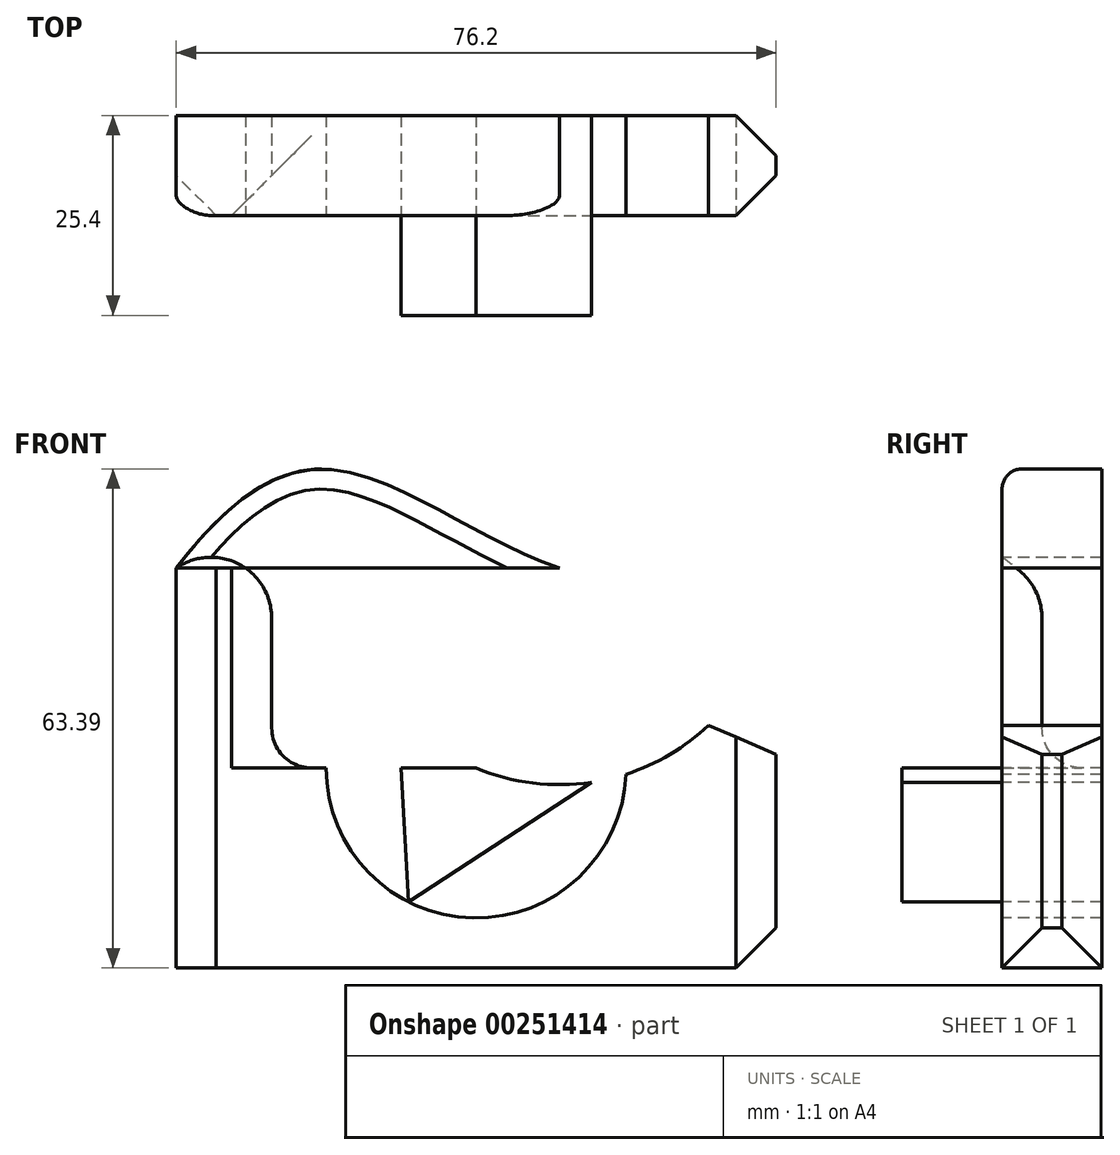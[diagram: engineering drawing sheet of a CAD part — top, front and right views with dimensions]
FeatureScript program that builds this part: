
annotation { "Feature Type Name" : "Feature", "Feature Type Description" : "" }
export const myFeature = defineFeature(function(context is Context, id is Id, definition is map)
    precondition{}
    {
        {
            var Q0;
            Q0=qCreatedBy(makeId("Front.planeOp"),FACE);
            var sketch = newSketch(context, id + "F0", { "sketchPlane" : qUnion([Q0])});
            skLineSegment(sketch, "E0.bottom", {"start": v(0, 0) * mm, "end": v(-25.97, 0) * mm});
            skLineSegment(sketch, "E0.top", {"start": v(0, 19.05) * mm, "end": v(-25.97, 19.05) * mm});
            skLineSegment(sketch, "E0.left", {"start": v(0, 0) * mm, "end": v(0, 19.05) * mm});
            skLineSegment(sketch, "E0.right", {"start": v(-25.97, 0) * mm, "end": v(-25.97, 19.05) * mm});
            skLineSegment(sketch, "E1.bottom", {"start": v(-38.1, 25.4) * mm, "end": v(38.1, 25.4) * mm});
            skLineSegment(sketch, "E1.top", {"start": v(-38.1, -25.4) * mm, "end": v(38.1, -25.4) * mm});
            skLineSegment(sketch, "E1.left", {"start": v(-38.1, 25.4) * mm, "end": v(-38.1, -25.4) * mm});
            skLineSegment(sketch, "E1.right", {"start": v(38.1, 25.4) * mm, "end": v(38.1, -25.4) * mm});
            skPoint(sketch, "E1.middle", {"position": v(0, 0) * mm});
            skCircle(sketch, "E2", {"center": v(0, 0) * mm, "radius": 19.05 * mm});
            skArc(sketch, "E3", {"start": v(0, 0) * mm, "mid": v(25.85, 2.5) * mm, "end": v(38.1, 25.4) * mm});
            skFitSpline(sketch, "E4", {"points": [v(-38.1, 25.4) * mm, v(-18.99, 37.97) * mm, v(10.58, 25.4) * mm, v(38.1, 25.4) * mm], "startDerivative": vector(56.09, 72.13) * mm, "endDerivative": vector(78.9, 16.08) * mm});
            skArc(sketch, "E5", {"start": v(-25.97, 19.05) * mm, "mid": v(-30.11, 25.9) * mm, "end": v(-38.1, 25.4) * mm});
            skCircle(sketch, "E6.cCircle", {"center": v(0, 0) * mm, "radius": 19.05 * mm, "construction": true});
            skLineSegment(sketch, "E6.0", {"start": v(19.02, 1.05) * mm, "end": v(-8.6, -17) * mm});
            skLineSegment(sketch, "E6.1", {"start": v(-8.6, -17) * mm, "end": v(-10.42, 15.95) * mm});
            skLineSegment(sketch, "E6.2", {"start": v(-10.42, 15.95) * mm, "end": v(19.02, 1.05) * mm});
            skSolve(sketch);
        }
        {
            var Q0;
            {var subQ1=sQuery(id+"F0.wireOp",EDGE,"E0.bottom");var subQ3=sQuery(id+"F0.wireOp",EDGE,"E6.1");var subQ4=makeQuery(id+"F0.imprint","INTERSECT",VERTEX,{"derivedFrom":[subQ1,subQ3]});Q0=makeQuery(id+"F0.imprint","IMPRINT",FACE,{"disambiguationData":[TD([[makeQuery(id+"F0.imprint","IMPRINT",EDGE,{"disambiguationData":[TD([[subQ4,1.0]])],"derivedFrom":subQ1}),1.0]])]});}
            var Q1;
            {var subQ5=sQuery(id+"F0.wireOp",EDGE,"E0.right");Q1=makeQuery(id+"F0.imprint","IMPRINT",FACE,{"disambiguationData":[TD([[makeQuery(id+"F0.imprint","IMPRINT",EDGE,{"derivedFrom":subQ5}),1.0]])]});}
            var Q2;
            {var subQ0=sQuery(id+"F0.wireOp",EDGE,"E4");var subQ1=sQuery(id+"F0.wireOp",EDGE,"E1.bottom");var subQ2=makeQuery(id+"F0.imprint","INTERSECT",VERTEX,{"derivedFrom":[subQ1,subQ0]});Q2=makeQuery(id+"F0.imprint","IMPRINT",FACE,{"disambiguationData":[TD([[makeQuery(id+"F0.imprint","IMPRINT",EDGE,{"disambiguationData":[TD([[subQ2,1.0]])],"derivedFrom":subQ1}),1.0]])]});}
            extrude(context, id + "F1", {"entities" : qUnion([Q0, Q1, Q2]), "oppositeDirection" : true, "depth" : 12.7 * mm});
        }
        {
            var Q0;
            Q0=makeQuery(id+"F1.opExtrude","CAP_FACE",FACE,{"disambiguationData":[OSD([sQuery(id+"F0.wireOp",EDGE,"E0.bottom"),sQuery(id+"F0.wireOp",EDGE,"E3"),sQuery(id+"F0.wireOp",EDGE,"E6.0"),sQuery(id+"F0.wireOp",EDGE,"E6.1")])],"isStart":false});
            extrude(context, id + "F2", {"entities" : qUnion([Q0]), "operationType" : NewBodyOperationType.ADD, "oppositeDirection" : true, "depth" : 25.4 * mm});
        }
        {
            var Q0;
            Q0=makeQuery(id+"F1.opExtrude","CAP_EDGE",EDGE,{"disambiguationData":[OSD([sQuery(id+"F0.wireOp",EDGE,"E4")])],"isStart":true});
            fillet(context, id + "F3", {"entities" : qUnion([Q0]), "radius" : 2.54 * mm, "tangentPropagation" : true, "allowEdgeOverflow" : false});
        }
        {
            var Q0;
            Q0=makeQuery(id+"F1.opExtrude","SWEPT_FACE",FACE,{"disambiguationData":[OSD([sQuery(id+"F0.wireOp",EDGE,"E1.right")])]});
            var Q1;
            Q1=makeQuery(id+"F1.opExtrude","CAP_EDGE",EDGE,{"disambiguationData":[OSD([sQuery(id+"F0.wireOp",EDGE,"E1.right")])],"isStart":false});
            var Q2;
            {var subQ0=sQuery(id+"F0.wireOp",EDGE,"E5");Q2=makeQuery(id+"F1.opExtrude","CAP_EDGE",EDGE,{"disambiguationData":[OSD([subQ0]),TDD([makeQuery(id+"F0.imprint","IMPRINT",EDGE,{"disambiguationData":[TD([[makeQuery(id+"F0.imprint","INTERSECT",VERTEX,{"derivedFrom":[sQuery(id+"F0.wireOp",EDGE,"E1.bottom"),subQ0]}),1.0]])],"derivedFrom":subQ0})])],"isStart":true});}
            chamfer(context, id + "F4", {"entities" : qUnion([Q0, Q1, Q2]), "width" : 5.08 * mm, "tangentPropagation" : true});
        }
        {
            var Q0;
            Q0=makeQuery(id+"F1.opExtrude","CAP_EDGE",EDGE,{"disambiguationData":[OSD([sQuery(id+"F0.wireOp",EDGE,"E1.left")])],"isStart":true});
            chamfer(context, id + "F5", {"entities" : qUnion([Q0]), "width" : 5.08 * mm, "tangentPropagation" : true});
        }
        {
            var Q0;
            Q0=makeQuery(id+"F1.opExtrude","SWEPT_EDGE",EDGE,{"disambiguationData":[OSD([sQuery(id+"F0.wireOp",EDGE,"E0.bottom"),sQuery(id+"F0.wireOp",EDGE,"E0.right")])]});
            fillet(context, id + "F6", {"entities" : qUnion([Q0]), "radius" : 5.08 * mm, "tangentPropagation" : true, "allowEdgeOverflow" : false});
        }
    });
